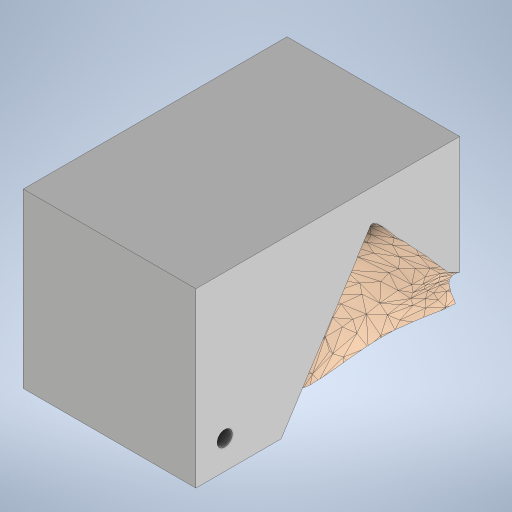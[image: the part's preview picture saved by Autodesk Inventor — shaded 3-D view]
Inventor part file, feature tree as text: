
AUTODESK INVENTOR PART (.ipt)
format: ipt  version: 2024 (Build 280153000, 153)  size: 10,728,960 bytes
history: native  units: mm
features: other x6, sketch x6, extrude x5, plane x2
ambient origin geometry x8: Origin, YZ Plane, XZ Plane, XY Plane, X Axis, Y Axis, Z Axis, Center Point
bodies: Body1 (feature_tree)
feature tree (19):
  other  "M.ipt"
  plane  "Plano de trabajo1"
  extrude  "Extrusión1"  [1 undecoded]
  other  "Combinar1"
  sketch  "Boceto3"  dims[d2=550.0mm d3=520.0mm]
  sketch  "Boceto4"  dims[d4=550.0mm d5=0.0mm d6=129.8482mm]
  plane  "Plano de trabajo2"
  sketch  "Boceto5"  dims[d17=180.0mm d18=180.0mm]
  extrude  "Extrusión2"  Depth=520.0mm
  extrude  "Extrusión3"  Depth=129.8482mm
  extrude  "Extrusión4"  Depth=180.0mm
  extrude  "Extrusión5"  Depth=180.0mm
  other  "Sólido1::M.ipt"
  other  "OperaciónIdentificador1"
  sketch  "Boceto1"  dims[d0=25.0mm d1=-365.0mm]
  other  "Sólido2"
  sketch  "Boceto6"  dims[d22=326.0mm d23=180.0mm]
  sketch  "Boceto7"  dims[d24=180.0mm d25=180.0mm d26=10.0mm d27=0.0mm d28=10.0mm d29=0.0mm d30=30.0mm d31=30.0mm d32=16.0mm d33=16.0mm d34=0.0mm d35=30.0mm d36=30.0mm d37=16.0mm d38=16.0mm d39=0.0mm d14=0.5mm d15=0.872665mm d16=0.5mm d19=0.5mm d20=0.872665mm d21=0.5mm]
  other  "Sólido1"
note: 1 required parameter value undecoded (feature->parameter linkage not recoverable at this tier; creation-order binding heuristic only, values carry confidence <= 0.55)
